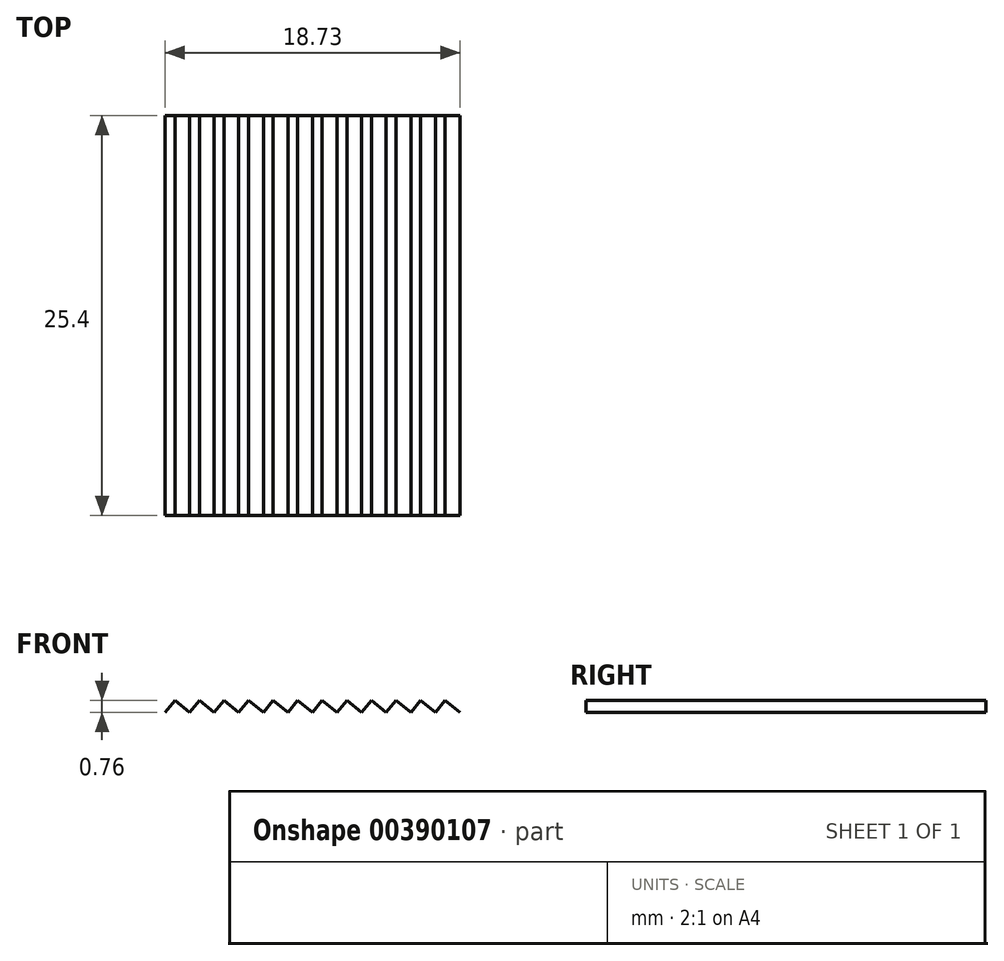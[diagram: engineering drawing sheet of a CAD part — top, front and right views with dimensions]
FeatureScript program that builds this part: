
annotation { "Feature Type Name" : "Feature", "Feature Type Description" : "" }
export const myFeature = defineFeature(function(context is Context, id is Id, definition is map)
    precondition{}
    {
        {
            var Q0;
            Q0=qCreatedBy(makeId("Front.planeOp"),FACE);
            var sketch = newSketch(context, id + "F0", { "sketchPlane" : qUnion([Q0])});
            skLineSegment(sketch, "E0", {"start": v(-76.1, 0) * mm, "end": v(-75.48, 0.76) * mm});
            skLineSegment(sketch, "E1", {"start": v(-75.48, 0.76) * mm, "end": v(-74.54, 0) * mm});
            skLineSegment(sketch, "E2", {"start": v(-74.54, 0) * mm, "end": v(-73.92, 0.76) * mm});
            skLineSegment(sketch, "E3", {"start": v(-73.92, 0.76) * mm, "end": v(-72.98, 0) * mm});
            skLineSegment(sketch, "E4", {"start": v(-72.98, 0) * mm, "end": v(-72.36, 0.76) * mm});
            skLineSegment(sketch, "E5", {"start": v(-72.36, 0.76) * mm, "end": v(-71.42, 0) * mm});
            skLineSegment(sketch, "E6", {"start": v(-71.42, 0) * mm, "end": v(-70.8, 0.76) * mm});
            skLineSegment(sketch, "E7", {"start": v(-70.8, 0.76) * mm, "end": v(-69.86, 0) * mm});
            skLineSegment(sketch, "E8", {"start": v(-69.86, 0) * mm, "end": v(-69.24, 0.76) * mm});
            skLineSegment(sketch, "E9", {"start": v(-69.24, 0.76) * mm, "end": v(-68.3, 0) * mm});
            skLineSegment(sketch, "E10", {"start": v(-68.3, 0) * mm, "end": v(-67.68, 0.76) * mm});
            skLineSegment(sketch, "E11", {"start": v(-67.68, 0.76) * mm, "end": v(-66.74, 0) * mm});
            skLineSegment(sketch, "E12", {"start": v(-66.74, 0) * mm, "end": v(-66.12, 0.76) * mm});
            skLineSegment(sketch, "E13", {"start": v(-66.12, 0.76) * mm, "end": v(-65.18, 0) * mm});
            skLineSegment(sketch, "E14", {"start": v(-65.18, 0) * mm, "end": v(-64.56, 0.76) * mm});
            skLineSegment(sketch, "E15", {"start": v(-64.56, 0.76) * mm, "end": v(-63.62, 0) * mm});
            skLineSegment(sketch, "E16", {"start": v(-63.62, 0) * mm, "end": v(-63, 0.76) * mm});
            skLineSegment(sketch, "E17", {"start": v(-63, 0.76) * mm, "end": v(-62.06, 0) * mm});
            skLineSegment(sketch, "E18", {"start": v(-62.06, 0) * mm, "end": v(-61.43, 0.76) * mm});
            skLineSegment(sketch, "E19", {"start": v(-61.43, 0.76) * mm, "end": v(-60.5, 0) * mm});
            skLineSegment(sketch, "E20", {"start": v(-60.5, 0) * mm, "end": v(-59.87, 0.76) * mm});
            skLineSegment(sketch, "E21", {"start": v(-59.87, 0.76) * mm, "end": v(-58.94, 0) * mm});
            skLineSegment(sketch, "E22", {"start": v(-58.94, 0) * mm, "end": v(-58.31, 0.76) * mm});
            skLineSegment(sketch, "E23", {"start": v(-58.31, 0.76) * mm, "end": v(-57.37, 0) * mm});
            skSolve(sketch);
        }
        {
            var Q0;
            Q0=sQuery(id+"F0.wireOp",EDGE,"E0");
            var Q1;
            Q1=sQuery(id+"F0.wireOp",EDGE,"E23");
            var Q2;
            Q2=sQuery(id+"F0.wireOp",EDGE,"E21");
            var Q3;
            Q3=sQuery(id+"F0.wireOp",EDGE,"E19");
            var Q4;
            Q4=sQuery(id+"F0.wireOp",EDGE,"E13");
            var Q5;
            Q5=sQuery(id+"F0.wireOp",EDGE,"E17");
            var Q6;
            Q6=sQuery(id+"F0.wireOp",EDGE,"E14");
            var Q7;
            Q7=sQuery(id+"F0.wireOp",EDGE,"E15");
            var Q8;
            Q8=sQuery(id+"F0.wireOp",EDGE,"E1");
            var Q9;
            Q9=sQuery(id+"F0.wireOp",EDGE,"E2");
            var Q10;
            Q10=sQuery(id+"F0.wireOp",EDGE,"E3");
            var Q11;
            Q11=sQuery(id+"F0.wireOp",EDGE,"E4");
            var Q12;
            Q12=sQuery(id+"F0.wireOp",EDGE,"E5");
            var Q13;
            Q13=sQuery(id+"F0.wireOp",EDGE,"E6");
            var Q14;
            Q14=sQuery(id+"F0.wireOp",EDGE,"E7");
            var Q15;
            Q15=sQuery(id+"F0.wireOp",EDGE,"E8");
            var Q16;
            Q16=sQuery(id+"F0.wireOp",EDGE,"E9");
            var Q17;
            Q17=sQuery(id+"F0.wireOp",EDGE,"E10");
            var Q18;
            Q18=sQuery(id+"F0.wireOp",EDGE,"E11");
            var Q19;
            Q19=sQuery(id+"F0.wireOp",EDGE,"E12");
            var Q20;
            Q20=sQuery(id+"F0.wireOp",EDGE,"E22");
            var Q21;
            Q21=sQuery(id+"F0.wireOp",EDGE,"E20");
            var Q22;
            Q22=sQuery(id+"F0.wireOp",EDGE,"E18");
            var Q23;
            Q23=sQuery(id+"F0.wireOp",EDGE,"E16");
            extrude(context, id + "F1", {"bodyType" : ToolBodyType.SURFACE, "surfaceEntities" : qUnion([Q0, Q1, Q2, Q3, Q4, Q5, Q6, Q7, Q8, Q9, Q10, Q11, Q12, Q13, Q14, Q15, Q16, Q17, Q18, Q19, Q20, Q21, Q22, Q23]), "depth" : 25.4 * mm});
        }
    });
